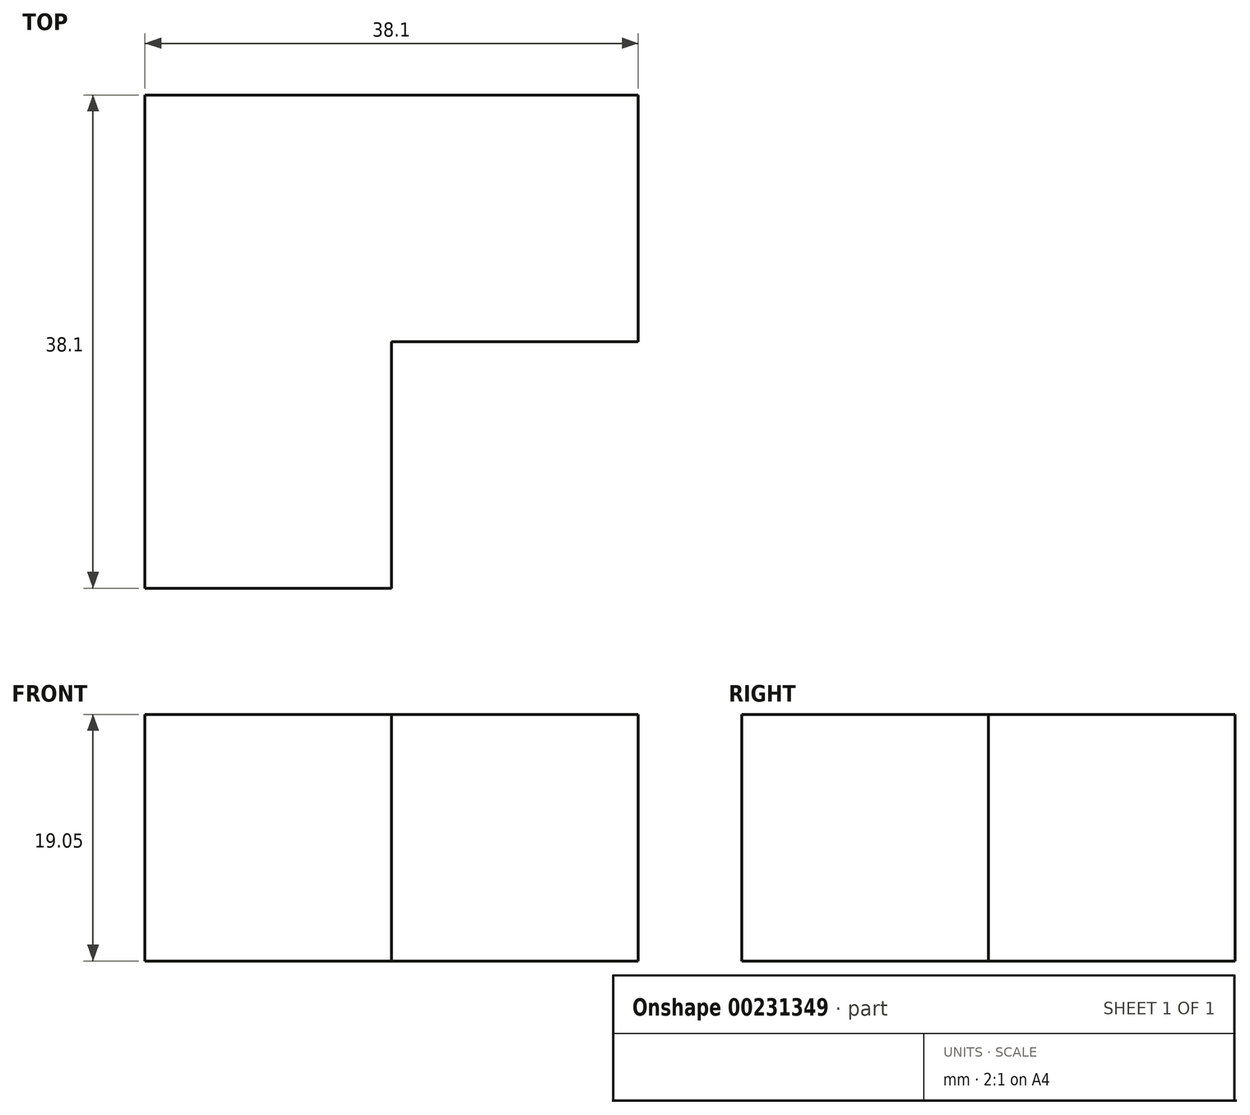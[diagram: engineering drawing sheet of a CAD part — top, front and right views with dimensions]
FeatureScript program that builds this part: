
annotation { "Feature Type Name" : "Feature", "Feature Type Description" : "" }
export const myFeature = defineFeature(function(context is Context, id is Id, definition is map)
    precondition{}
    {
        {
            var Q0;
            Q0=qCreatedBy(makeId("Front.planeOp"),FACE);
            var sketch = newSketch(context, id + "F0", { "sketchPlane" : qUnion([Q0])});
            skLineSegment(sketch, "E0.bottom", {"start": v(-35.12, 36.75) * mm, "end": v(-16.07, 36.75) * mm});
            skLineSegment(sketch, "E0.top", {"start": v(-35.12, 17.7) * mm, "end": v(-16.07, 17.7) * mm});
            skLineSegment(sketch, "E0.left", {"start": v(-35.12, 36.75) * mm, "end": v(-35.12, 17.7) * mm});
            skLineSegment(sketch, "E0.right", {"start": v(-16.07, 36.75) * mm, "end": v(-16.07, 17.7) * mm});
            skLineSegment(sketch, "E1.bottom", {"start": v(-16.07, 36.75) * mm, "end": v(2.98, 36.75) * mm});
            skLineSegment(sketch, "E1.top", {"start": v(-16.07, 17.7) * mm, "end": v(2.98, 17.7) * mm});
            skLineSegment(sketch, "E1.right", {"start": v(2.98, 36.75) * mm, "end": v(2.98, 17.7) * mm});
            skSolve(sketch);
        }
        {
            var Q0;
            Q0 = qSketchRegion(id + "F0", true);
            extrude(context, id + "F1", {"entities" : qUnion([Q0]), "depth" : 38.1 * mm});
        }
        {
            var Q0;
            Q0=makeQuery(id+"F0.imprint","IMPRINT",FACE,{"disambiguationData":[TD([[makeQuery(id+"F0.imprint","IMPRINT",EDGE,{"derivedFrom":sQuery(id+"F0.wireOp",EDGE,"E1.bottom")}),-1.0]])]});
            extrude(context, id + "F2", {"entities" : qUnion([Q0]), "operationType" : NewBodyOperationType.ADD, "depth" : 19.05 * mm});
        }
        {
            var Q0;
            Q0=makeQuery(id+"F1.opExtrude","SWEPT_FACE",FACE,{"disambiguationData":[OSD([sQuery(id+"F0.wireOp",EDGE,"E0.bottom"),sQuery(id+"F0.wireOp",EDGE,"E1.bottom")])]});
            var sketch = newSketch(context, id + "F3", { "sketchPlane" : qUnion([Q0])});
            skLineSegment(sketch, "E2.bottom", {"start": v(-16.07, -38.1) * mm, "end": v(2.98, -38.1) * mm});
            skLineSegment(sketch, "E2.top", {"start": v(-16.07, -19.05) * mm, "end": v(2.98, -19.05) * mm});
            skLineSegment(sketch, "E2.left", {"start": v(-16.07, -38.1) * mm, "end": v(-16.07, -19.05) * mm});
            skLineSegment(sketch, "E2.right", {"start": v(2.98, -38.1) * mm, "end": v(2.98, -19.05) * mm});
            skSolve(sketch);
        }
        {
            var Q0;
            Q0=makeQuery(id+"F3.imprint","IMPRINT",FACE,{"disambiguationData":[TD([[makeQuery(id+"F3.imprint","IMPRINT",EDGE,{"derivedFrom":sQuery(id+"F3.wireOp",EDGE,"E2.bottom")}),1.0]])]});
            extrude(context, id + "F4", {"entities" : qUnion([Q0]), "operationType" : NewBodyOperationType.REMOVE, "oppositeDirection" : true, "depth" : 25.4 * mm});
        }
    });
